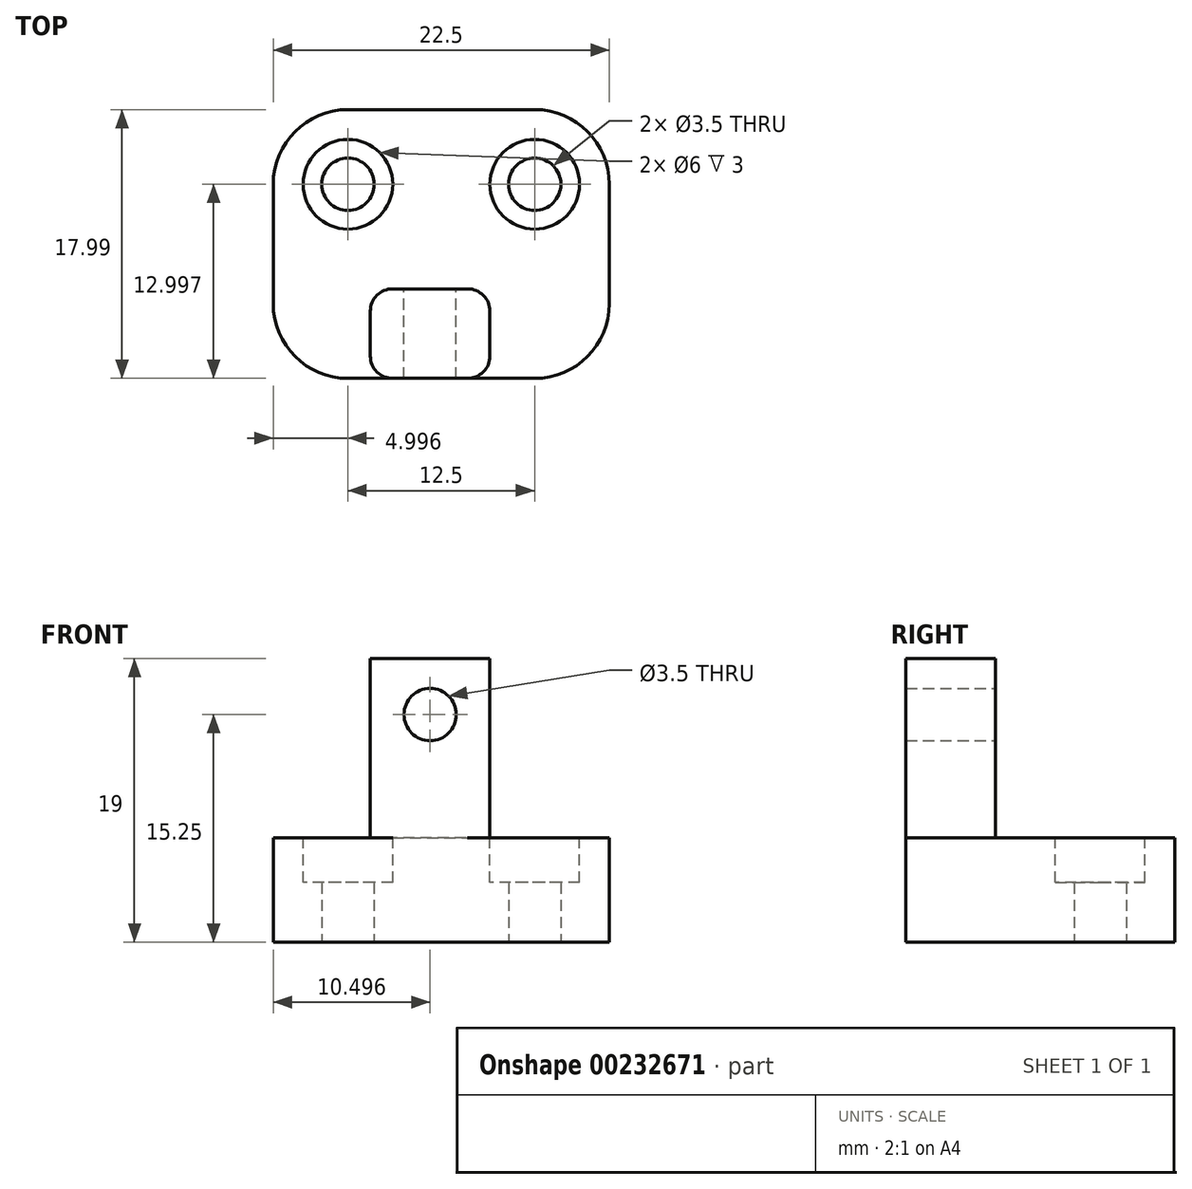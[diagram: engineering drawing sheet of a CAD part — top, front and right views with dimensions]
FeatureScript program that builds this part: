
annotation { "Feature Type Name" : "Feature", "Feature Type Description" : "" }
export const myFeature = defineFeature(function(context is Context, id is Id, definition is map)
    precondition{}
    {
        {
            var Q0;
            Q0=qCreatedBy(makeId("Top.planeOp"),FACE);
            var sketch = newSketch(context, id + "F0", { "sketchPlane" : qUnion([Q0])});
            skCircle(sketch, "E0", {"center": v(-50.98, 33.93) * mm, "radius": 1.75 * mm});
            skPoint(sketch, "E1", {"position": v(-38.48, 33.93) * mm});
            skCircle(sketch, "E2", {"center": v(-50.98, 33.93) * mm, "radius": 3 * mm});
            skLineSegment(sketch, "E3", {"start": v(-51.14, 36.92) * mm, "end": v(-51.14, 38.92) * mm});
            skLineSegment(sketch, "E4", {"start": v(-53.98, 33.93) * mm, "end": v(-55.98, 33.93) * mm});
            skLineSegment(sketch, "E5.bottom", {"start": v(-35.98, 28.93) * mm, "end": v(-55.98, 28.93) * mm});
            skLineSegment(sketch, "E5.top", {"start": v(-35.98, 38.92) * mm, "end": v(-55.98, 38.92) * mm});
            skLineSegment(sketch, "E5.right", {"start": v(-55.98, 28.93) * mm, "end": v(-55.98, 38.92) * mm});
            skPoint(sketch, "E6", {"position": v(-53.98, 29.93) * mm});
            skPoint(sketch, "E7", {"position": v(-53.98, 25.93) * mm});
            skLineSegment(sketch, "E8", {"start": v(-55.98, 28.93) * mm, "end": v(-55.98, 25.93) * mm});
            skLineSegment(sketch, "E9", {"start": v(-55.98, 25.93) * mm, "end": v(-53.98, 25.93) * mm});
            skLineSegment(sketch, "E10", {"start": v(-53.98, 25.93) * mm, "end": v(-43.98, 25.93) * mm});
            skLineSegment(sketch, "E11", {"start": v(-43.98, 25.93) * mm, "end": v(-35.98, 25.93) * mm});
            skLineSegment(sketch, "E12", {"start": v(-35.98, 25.93) * mm, "end": v(-35.98, 28.93) * mm});
            skCircle(sketch, "E13", {"center": v(-38.48, 33.93) * mm, "radius": 1.75 * mm});
            skCircle(sketch, "E14", {"center": v(-38.48, 33.93) * mm, "radius": 3 * mm});
            skLineSegment(sketch, "E15", {"start": v(-35.48, 33.93) * mm, "end": v(-33.48, 33.93) * mm});
            skLineSegment(sketch, "E16", {"start": v(-33.48, 33.93) * mm, "end": v(-33.48, 38.92) * mm});
            skLineSegment(sketch, "E17", {"start": v(-33.48, 38.92) * mm, "end": v(-35.98, 38.92) * mm});
            skLineSegment(sketch, "E18", {"start": v(-33.48, 33.93) * mm, "end": v(-33.48, 25.93) * mm});
            skLineSegment(sketch, "E19", {"start": v(-33.48, 25.93) * mm, "end": v(-35.98, 25.93) * mm});
            skSolve(sketch);
        }
        {
            var Q0;
            Q0 = qSketchRegion(id + "F0", true);
            var Q1;
            Q1=makeQuery(id+"F0.imprint","IMPRINT",FACE,{"disambiguationData":[TD([[makeQuery(id+"F0.imprint","IMPRINT",EDGE,{"derivedFrom":sQuery(id+"F0.wireOp",EDGE,"T3ExR0Pi-24DN-FC4z-355n-9pyuhfceIKFL")}),-1.0]])]});
            var Q2;
            Q2=makeQuery(id+"F0.imprint","IMPRINT",FACE,{"disambiguationData":[TD([[makeQuery(id+"F0.imprint","IMPRINT",EDGE,{"derivedFrom":sQuery(id+"F0.wireOp",EDGE,"E0")}),-1.0]])]});
            var Q3;
            Q3=makeQuery(id+"F0.imprint","IMPRINT",FACE,{"disambiguationData":[TD([[makeQuery(id+"F0.imprint","IMPRINT",EDGE,{"derivedFrom":sQuery(id+"F0.wireOp",EDGE,"E13")}),-1.0]])]});
            extrude(context, id + "F1", {"entities" : qUnion([Q0, Q1, Q2, Q3]), "depth" : 7 * mm});
        }
        {
            var Q0;
            Q0=makeQuery(id+"F1.opExtrude","CAP_FACE",FACE,{"disambiguationData":[OSD([sQuery(id+"F0.wireOp",EDGE,"E0"),sQuery(id+"F0.wireOp",EDGE,"T3ExR0Pi-24DN-FC4z-355n-9pyuhfceIKFL"),sQuery(id+"F0.wireOp",EDGE,"E5.top"),sQuery(id+"F0.wireOp",EDGE,"E5.left"),sQuery(id+"F0.wireOp",EDGE,"E5.right"),sQuery(id+"F0.wireOp",EDGE,"E8"),sQuery(id+"F0.wireOp",EDGE,"E9"),sQuery(id+"F0.wireOp",EDGE,"E10"),sQuery(id+"F0.wireOp",EDGE,"E11"),sQuery(id+"F0.wireOp",EDGE,"E12")])],"isStart":false});
            var sketch = newSketch(context, id + "F2", { "sketchPlane" : qUnion([Q0])});
            skPoint(sketch, "E20", {"position": v(-50.98, 33.93) * mm});
            skCircle(sketch, "E21", {"center": v(-50.98, 33.93) * mm, "radius": 3 * mm});
            skCircle(sketch, "E22", {"center": v(-38.48, 33.93) * mm, "radius": 3 * mm});
            skSolve(sketch);
        }
        {
            var Q0;
            Q0=makeQuery(id+"F1.opExtrude","SWEPT_FACE",FACE,{"disambiguationData":[OSD([sQuery(id+"F0.wireOp",EDGE,"E9"),sQuery(id+"F0.wireOp",EDGE,"E10"),sQuery(id+"F0.wireOp",EDGE,"E11")])]});
            extrude(context, id + "F3", {"entities" : qUnion([Q0]), "operationType" : NewBodyOperationType.ADD, "depth" : 5 * mm});
        }
        {
            var Q0;
            {var subQ0=sQuery(id+"F0.wireOp",EDGE,"E11");var subQ1=sQuery(id+"F0.wireOp",EDGE,"E10");var subQ2=sQuery(id+"F0.wireOp",EDGE,"E9");Q0=makeQuery(id+"F3.boolean.opBoolean","MERGE",FACE,{"derivedFrom":[makeQuery(id+"F1.opExtrude","CAP_FACE",FACE,{"disambiguationData":[OSD([sQuery(id+"F0.wireOp",EDGE,"E0"),sQuery(id+"F0.wireOp",EDGE,"T3ExR0Pi-24DN-FC4z-355n-9pyuhfceIKFL"),sQuery(id+"F0.wireOp",EDGE,"E5.top"),sQuery(id+"F0.wireOp",EDGE,"E5.left"),sQuery(id+"F0.wireOp",EDGE,"E5.right"),sQuery(id+"F0.wireOp",EDGE,"E8"),subQ2,subQ1,subQ0,sQuery(id+"F0.wireOp",EDGE,"E12")])],"isStart":false}),makeQuery(id+"F3.opExtrude","SWEPT_FACE",FACE,{"disambiguationData":[OSD([subQ2,subQ1,subQ0]),TDD([makeQuery(id+"F1.opExtrude","CAP_EDGE",EDGE,{"disambiguationData":[OSD([subQ2,subQ1,subQ0])],"isStart":false})])]})]});}
            var sketch = newSketch(context, id + "F4", { "sketchPlane" : qUnion([Q0])});
            skLineSegment(sketch, "E23", {"start": v(-41.48, 20.93) * mm, "end": v(-49.48, 20.93) * mm});
            skLineSegment(sketch, "E24", {"start": v(-49.48, 20.93) * mm, "end": v(-49.48, 26.93) * mm});
            skLineSegment(sketch, "E25", {"start": v(-49.48, 26.93) * mm, "end": v(-41.48, 26.93) * mm});
            skLineSegment(sketch, "E26", {"start": v(-41.48, 26.93) * mm, "end": v(-41.48, 20.93) * mm});
            skSolve(sketch);
        }
        {
            var Q0;
            Q0 = qSketchRegion(id + "F4", true);
            extrude(context, id + "F5", {"entities" : qUnion([Q0]), "operationType" : NewBodyOperationType.ADD, "depth" : 12 * mm});
        }
        {
            var Q0;
            Q0=makeQuery(id+"F5.opExtrude","SWEPT_EDGE",EDGE,{"disambiguationData":[OSD([sQuery(id+"F0.wireOp",EDGE,"E9"),sQuery(id+"F0.wireOp",EDGE,"E10"),sQuery(id+"F0.wireOp",EDGE,"E11"),sQuery(id+"F0.wireOp",EDGE,"E19"),sQuery(id+"F4.wireOp",EDGE,"E23"),sQuery(id+"F4.wireOp",EDGE,"E24")])]});
            var Q1;
            Q1=makeQuery(id+"F5.opExtrude","SWEPT_EDGE",EDGE,{"disambiguationData":[OSD([sQuery(id+"F0.wireOp",EDGE,"E9"),sQuery(id+"F0.wireOp",EDGE,"E10"),sQuery(id+"F0.wireOp",EDGE,"E11"),sQuery(id+"F0.wireOp",EDGE,"E19"),sQuery(id+"F4.wireOp",EDGE,"E23"),sQuery(id+"F4.wireOp",EDGE,"E26")])]});
            var Q2;
            Q2=makeQuery(id+"F5.opExtrude","SWEPT_EDGE",EDGE,{"disambiguationData":[OSD([sQuery(id+"F4.wireOp",EDGE,"E24"),sQuery(id+"F4.wireOp",EDGE,"E25")])]});
            var Q3;
            Q3=makeQuery(id+"F5.opExtrude","SWEPT_EDGE",EDGE,{"disambiguationData":[OSD([sQuery(id+"F4.wireOp",EDGE,"E25"),sQuery(id+"F4.wireOp",EDGE,"E26")])]});
            fillet(context, id + "F6", {"entities" : qUnion([Q0, Q1, Q2, Q3]), "radius" : 1.5 * mm, "tangentPropagation" : true, "allowEdgeOverflow" : false});
        }
        {
            var Q0;
            Q0=makeQuery(id+"F2.imprint","IMPRINT",FACE,{"disambiguationData":[TD([[makeQuery(id+"F2.imprint","IMPRINT",EDGE,{"derivedFrom":sQuery(id+"F2.wireOp",EDGE,"E21")}),1.0]])]});
            var Q1;
            Q1=makeQuery(id+"F2.imprint","IMPRINT",FACE,{"disambiguationData":[TD([[makeQuery(id+"F2.imprint","IMPRINT",EDGE,{"derivedFrom":sQuery(id+"F2.wireOp",EDGE,"E22")}),1.0]])]});
            extrude(context, id + "F7", {"entities" : qUnion([Q0, Q1]), "operationType" : NewBodyOperationType.REMOVE, "oppositeDirection" : true, "depth" : 3 * mm});
        }
        {
            var Q0;
            Q0=makeQuery(id+"F3.opExtrude","CAP_EDGE",EDGE,{"disambiguationData":[OSD([sQuery(id+"F0.wireOp",EDGE,"E8"),sQuery(id+"F0.wireOp",EDGE,"E9")])],"isStart":false});
            var Q1;
            Q1=makeQuery(id+"F1.opExtrude","SWEPT_EDGE",EDGE,{"disambiguationData":[OSD([sQuery(id+"F0.wireOp",EDGE,"E5.top"),sQuery(id+"F0.wireOp",EDGE,"E5.right")])]});
            var Q2;
            Q2=makeQuery(id+"F1.opExtrude","SWEPT_EDGE",EDGE,{"disambiguationData":[OSD([sQuery(id+"F0.wireOp",EDGE,"E16"),sQuery(id+"F0.wireOp",EDGE,"E17")])]});
            var Q3;
            Q3=makeQuery(id+"F3.opExtrude","CAP_EDGE",EDGE,{"disambiguationData":[OSD([sQuery(id+"F0.wireOp",EDGE,"E18"),sQuery(id+"F0.wireOp",EDGE,"E19")])],"isStart":false});
            fillet(context, id + "F8", {"entities" : qUnion([Q0, Q1, Q2, Q3]), "radius" : 5 * mm, "tangentPropagation" : true, "allowEdgeOverflow" : false});
        }
        {
            var Q0;
            Q0=makeQuery(id+"F5.opExtrude","SWEPT_FACE",FACE,{"disambiguationData":[OSD([sQuery(id+"F4.wireOp",EDGE,"E25")])]});
            var sketch = newSketch(context, id + "F9", { "sketchPlane" : qUnion([Q0])});
            skLineSegment(sketch, "E27", {"start": v(45.48, 19) * mm, "end": v(45.48, 17) * mm});
            skLineSegment(sketch, "E28", {"start": v(45.48, 17) * mm, "end": v(45.48, 15.25) * mm});
            skCircle(sketch, "E29", {"center": v(45.48, 15.25) * mm, "radius": 1.75 * mm});
            skSolve(sketch);
        }
        {
            var Q0;
            Q0 = qSketchRegion(id + "F9", true);
            extrude(context, id + "F10", {"entities" : qUnion([Q0]), "operationType" : NewBodyOperationType.REMOVE, "oppositeDirection" : true, "depth" : 25 * mm});
        }
    });
